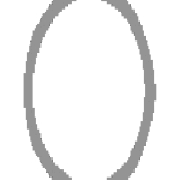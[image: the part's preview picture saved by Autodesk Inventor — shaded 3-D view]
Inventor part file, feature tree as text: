
AUTODESK INVENTOR PART (.ipt)
format: ipt  version: 2021 (Build 250183000, 183)  size: 112,128 bytes
history: native  units: in
note: dims shown in document units (in); Inventor stores cm internally (conversion verified against a paired STEP export)
features: other x4, sketch x3, plane x1
ambient origin geometry x8: Origin, YZ Plane, XZ Plane, XY Plane, X Axis, Y Axis, Z Axis, Center Point
bodies: Solid1 (feature_tree), Body (feature_tree)
feature tree (8):
  other  "Driven Length"
  other  "Frame Generator"
  other  "Start Plane"
  other  "End Plane"
  sketch  "Sketch"  dims[d2=20.2683in d4=-0.0in d5=20.2683in d6=0.12in d7=0.0in d8=90.0deg d9=20.2683in]
  sketch  "Sketch2"  dims[d0=1.0in]
  plane  "Work Plane3"
  sketch  "Sketch3"  dims[d1=0.065in]
